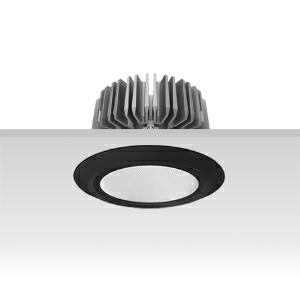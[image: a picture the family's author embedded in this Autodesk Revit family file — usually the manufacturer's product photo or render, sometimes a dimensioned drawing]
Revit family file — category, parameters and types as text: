
# Revit family: 3f_filippi_-_3f_reno_bianco_ampio_3f_filippi_-_30366_a01036_-_3f_reno_150_wh_3000-840_ep_wide___vs_bk_86e3
name_source: partatom
category: Lighting Fixtures
units: mm (PartAtom-declared; Revit-internal decimal feet)

## family parameters
Cut with Voids When Loaded = No
Host = Face
Light Source = No
Part Type = Normal
Room Calculation Point = No
Round Connector Dimension = Use Diameter
Shared = No

## types (1)
- 3F Filippi - 3F Reno Bianco Ampio (1 x LED, 2293 lm, 29 W, 4000 K)
    Apparent Load = 29 VA
    Approval mark = ENEC
    CIE Flux Codes = 74 93 99 100 100
    Color Rendering = 80
    Color Temperature = 4000 K
    Control Gear = Electronic ballast
    Default Elevation = 1800 mm
    Description = ILLUMINOTECHNICAL
Luminous efficiency 100% (DLOR 100%, ULOR 0%).
Initial luminous flux of the luminaire 2293 lm.
Emergency luminaire luminous flux BLF 14.3%.
Direct symmetric wide distribution.
Installation Interdistance Transv.D = 1.12 x hu - Long.D = 1.11 x hu.
Tabular UGR (CIE 117 - 4H-8H; S=0.25H; 70/50/20): RUG 23.9 - 23.7.
Beam angle: 74° - 73°.
Luminous efficacy 79 lm/W.
Lifetime (L90/B10): 30000 h. (tq+25°C)
Lifetime (L85/B10): 50000 h. (tq+25°C)
Lifetime (L70/B10): 80000 h. (tq+25°C)
Sudden decreased luminous flux after 50000 hours: 0% (C0).
Photobiological safety in compliance with IEC/TR 62778: RG0 risk exempt, (IEC 62471).
In compliance with IEC/EN 62722-2-1 - IEC/EN 62717 standards.

SOURCE
Compact LED module 3000/840.
Energy efficiency class (UE 2019/2020 - UE 2019/2015): D.
CIE 13.3 Colour rendering index: CRI >80 (R9 <50%).
IES TM-30 Fidelity Index: Rf = 84 Rg = 95.
CCT nominal colour temperature 4000 K.
Colour initial tolerance (MacAdam): SDCM 3.
Zhaga Book 3 compliant.

MECHANICAL
Passive heat dissipator in die-casting aluminium, oversized, for optimum thermal management of the LED module.
Parabolic element with graduated/concentric rings in white polycarbonate.
Transparent external lens with glossy and satin differentiated surfaces, with a cooling and anti-insect system in methacrylate (PMMA).
Fastening spring clips in stainless steel.
Dimensions: diameter 176 mm, height 111 mm. Weight 2 kg.
IP44 protection degree for exposed part, IP20 for recessed part.
Mechanical strength to impacts IK06 (1 joule).
Glow-wire test resistance 650°C.

ELECTRICAL
Wiring on a separate unit.
Halogen Free electronic wiring 230V-50/60Hz, power factor 0.90, THD <25%, constant output current, SELV, class II, 1 driver.
Power of the luminaire 29 W.
CE - IEC 60598-1 - EN 60598-1.
EP maintained emergency wiring on board, 1h duration, 24h recharge; compliant with EN 60598-2-22, excluding high risk areas.
SAFE FLICKER: PstLM=<1 and SVM=<0.4 (IEC TR 61547-1 and IEC TR 63158), to ensure a more comfortable and safe light.
Ambient temperature from +5°C to +25°C.
Temperature class T6 max 85°C.
Relative humidity UR: <85%.

INSTALLATION
Pull-up recessed fitting.
False ceiling carving: 150 mm.
All accessories dedicated to this product are available on the Catalog and on our website www.3F-Filippi.com.

ACCESSORIES
A01036 - Anti-glare microprismatic VS moulded glass, tempered, not flammable, locked and in line with the trim, in black polycarbonate.

APPLICATIONS
Environments: architectural, commercial, exhibition areas, transit areas, corridors, shops, display windows, service areas.
In false ceilings with narrow voids.

WARNING
Luminaire designed for disposal/recycling at end-of-life.
Replaceable (LED only) light source by a professional. Replaceable control gear by a professional.
    Height = 0 mm  [stored 0 ft]
    Lamp = 1 x LED
    Lamp Light Flux = 2293 lm
    Lamp Power = 29 W
    Lamp count = 1
    Length = 176 mm
    Lifetime = 50000 h
    Luminous efficacy = 79 lm/W
    Manufacturer = 3F Filippi
    ModVariant = No
    Model = 3F Filippi - 30366+A01036 - 3F Reno 150 WH 3000-840 EP WIDE + VS BK
    Mounting Place = Ceiling
    Mounting Type = Recessed
    Number of Poles = 1
    OnlyDefault = Yes
    Power Factor = 1
    Product Name = 3F Filippi - 3F Reno Bianco Ampio
    Product group = recessed luminaire
    ProductGroupID = 4
    Protection Class = Protection class II
    Protection Degree = IP 20
    RLX_Detail_Level = 1
    RLX_Emergency_Light_Flux = 0 lm
    RLX_Emergency_Type = 0
    RLX_Emergency_Type_DB = No
    RlxData = <blob elided: 85089 chars, md5=638a05e1>
    Socket = socket
    Standby Power = 0 W
    System Light Flux = 2293 lm
    System Power = 29 W
    Type Comments = Product without accessories
    Type Image = 3ffilippi_3f_reno_150_bk_vs_smp.jpg
    URL = http://relux.com
    VarID = ---
    Voltage = 0 V
    Weight = 0.00 kg
    Width = 0 mm  [stored 0 ft]

note: [stored X ft] marks values corroborated as IEEE doubles in the binary element streams (Revit-internal decimal feet)

## geometry (parser evidence)
native form markers: Blend x4, Sweep x10
no freeform markers — native parametric forms only
